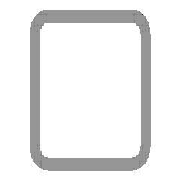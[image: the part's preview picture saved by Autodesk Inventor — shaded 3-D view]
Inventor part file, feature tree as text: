
AUTODESK INVENTOR PART (.ipt)
format: ipt  version: 2022 (Build 260153000, 153)  size: 149,504 bytes
history: native  units: mm (DEFAULTED — no unit token found)
features: other x4, plane x3, sketch x3, split x2
ambient origin geometry x8: Origin, YZ Plane, XZ Plane, XY Plane, X Axis, Y Axis, Z Axis, Center Point
bodies: Solid1 (feature_tree), Body (feature_tree)
feature tree (12):
  parser-record x1  (decoder bookkeeping rows leaked as tree rows — omitted from the tree; the rows remain in map.json)
  other  "Driven Length"
  other  "Start Plane"
  other  "End Plane"
  plane  "Work Plane4"
  split  "Split1"
  plane  "Work Plane5"
  split  "Split2"
  sketch  "Sketch"  dims[d7=8.0mm d9=40.0mm d11=40.0mm d12=4.0mm d13=-8.284271mm d14=90.0mm d15=20.0mm d16=20.0mm d17=90.0deg d18=98.284271mm]
  sketch  "Sketch3"  dims[d3=98.284271mm]
  plane  "Work Plane3"
  sketch  "Sketch4"  dims[d4=0.0mm]
